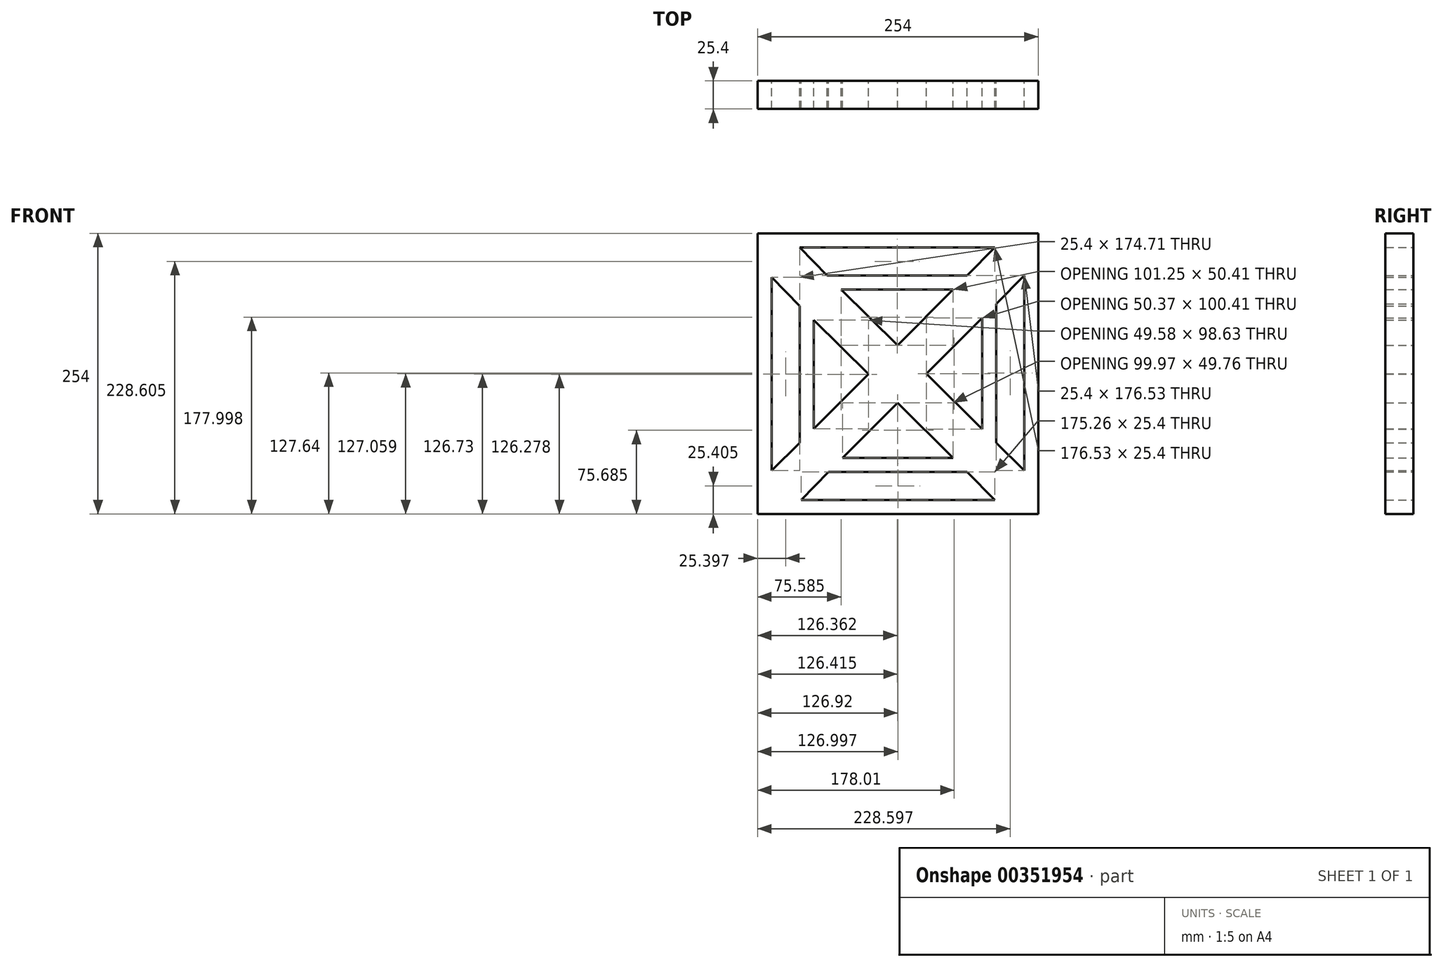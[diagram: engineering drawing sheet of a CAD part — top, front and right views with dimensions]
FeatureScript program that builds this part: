
annotation { "Feature Type Name" : "Feature", "Feature Type Description" : "" }
export const myFeature = defineFeature(function(context is Context, id is Id, definition is map)
    precondition{}
    {
        {
            var Q0;
            Q0=qCreatedBy(makeId("Front.planeOp"),FACE);
            var sketch = newSketch(context, id + "F0", { "sketchPlane" : qUnion([Q0])});
            skLineSegment(sketch, "E0.bottom", {"start": v(-189.74, 249.95) * mm, "end": v(64.26, 249.95) * mm});
            skLineSegment(sketch, "E0.top", {"start": v(-189.74, -4.05) * mm, "end": v(64.26, -4.05) * mm});
            skLineSegment(sketch, "E0.left", {"start": v(-189.74, 249.95) * mm, "end": v(-189.74, -4.05) * mm});
            skLineSegment(sketch, "E0.right", {"start": v(64.26, 249.95) * mm, "end": v(64.26, -4.05) * mm});
            skLineSegment(sketch, "E1.bottom", {"start": v(-151.64, 237.25) * mm, "end": v(24.89, 237.25) * mm});
            skLineSegment(sketch, "E1.top", {"start": v(-150.37, 8.65) * mm, "end": v(24.89, 8.65) * mm});
            skLineSegment(sketch, "E1.left", {"start": v(-177.04, 210.03) * mm, "end": v(-177.04, 35.32) * mm});
            skLineSegment(sketch, "E1.right", {"start": v(51.56, 211.85) * mm, "end": v(51.56, 35.32) * mm});
            skLineSegment(sketch, "E2.bottom", {"start": v(-126.76, 211.85) * mm, "end": v(0, 211.85) * mm});
            skLineSegment(sketch, "E2.top", {"start": v(-125.49, 34.05) * mm, "end": v(0, 34.05) * mm});
            skLineSegment(sketch, "E2.left", {"start": v(-151.64, 184.11) * mm, "end": v(-151.64, 60.21) * mm});
            skLineSegment(sketch, "E2.right", {"start": v(26.16, 185.93) * mm, "end": v(26.16, 60.21) * mm});
            skLineSegment(sketch, "E3.bottom", {"start": v(-113.95, 199.15) * mm, "end": v(-12.7, 199.15) * mm});
            skLineSegment(sketch, "E3.top", {"start": v(-112.8, 46.75) * mm, "end": v(-12.83, 46.75) * mm});
            skLineSegment(sketch, "E3.left", {"start": v(-138.94, 171.54) * mm, "end": v(-138.94, 72.91) * mm});
            skLineSegment(sketch, "E3.right", {"start": v(13.46, 173.21) * mm, "end": v(13.46, 72.8) * mm});
            skLineSegment(sketch, "E4", {"start": v(-177.04, 210.03) * mm, "end": v(-151.64, 184.11) * mm});
            skLineSegment(sketch, "E5", {"start": v(-151.64, 237.25) * mm, "end": v(-126.76, 211.85) * mm});
            skLineSegment(sketch, "E6", {"start": v(24.89, 237.25) * mm, "end": v(0, 211.85) * mm});
            skLineSegment(sketch, "E7", {"start": v(51.56, 211.85) * mm, "end": v(26.16, 185.93) * mm});
            skLineSegment(sketch, "E8", {"start": v(-151.64, 60.21) * mm, "end": v(-177.04, 35.32) * mm});
            skLineSegment(sketch, "E9", {"start": v(-125.49, 34.05) * mm, "end": v(-150.37, 8.65) * mm});
            skLineSegment(sketch, "E10", {"start": v(0, 34.05) * mm, "end": v(24.89, 8.65) * mm});
            skLineSegment(sketch, "E11", {"start": v(26.16, 60.21) * mm, "end": v(51.56, 35.32) * mm});
            skPoint(sketch, "E12.orphan", {"position": v(-151.64, 211.85) * mm});
            skPoint(sketch, "E13.orphan", {"position": v(-177.04, 237.25) * mm});
            skPoint(sketch, "E14.orphan", {"position": v(26.16, 211.85) * mm});
            skPoint(sketch, "E15.orphan", {"position": v(51.56, 237.25) * mm});
            skPoint(sketch, "E16.orphan", {"position": v(51.56, 8.65) * mm});
            skPoint(sketch, "E17.orphan", {"position": v(-177.04, 8.65) * mm});
            skLineSegment(sketch, "E18", {"start": v(-138.94, 171.54) * mm, "end": v(-89.37, 122.49) * mm});
            skLineSegment(sketch, "E19", {"start": v(-113.95, 199.15) * mm, "end": v(-63.11, 148.74) * mm});
            skLineSegment(sketch, "E20", {"start": v(-12.7, 199.15) * mm, "end": v(-63.11, 148.74) * mm});
            skLineSegment(sketch, "E21", {"start": v(-112.8, 46.75) * mm, "end": v(-63.12, 96.52) * mm});
            skLineSegment(sketch, "E22.trimOffspring", {"start": v(-63.12, 96.52) * mm, "end": v(-12.83, 46.75) * mm});
            skLineSegment(sketch, "E23.trimOffspring", {"start": v(-89.37, 122.49) * mm, "end": v(-138.94, 72.91) * mm});
            skLineSegment(sketch, "E24.trimOffspring", {"start": v(-36.92, 122.76) * mm, "end": v(13.46, 72.8) * mm});
            skLineSegment(sketch, "E25.trimOffspring", {"start": v(-36.92, 122.76) * mm, "end": v(13.46, 173.21) * mm});
            skSolve(sketch);
        }
        {
            var Q0;
            Q0=makeQuery(id+"F0.imprint","IMPRINT",FACE,{"disambiguationData":[TD([[makeQuery(id+"F0.imprint","IMPRINT",EDGE,{"derivedFrom":sQuery(id+"F0.wireOp",EDGE,"E0.bottom")}),-1.0]])]});
            extrude(context, id + "F1", {"entities" : qUnion([Q0]), "depth" : 25.4 * mm});
        }
    });
